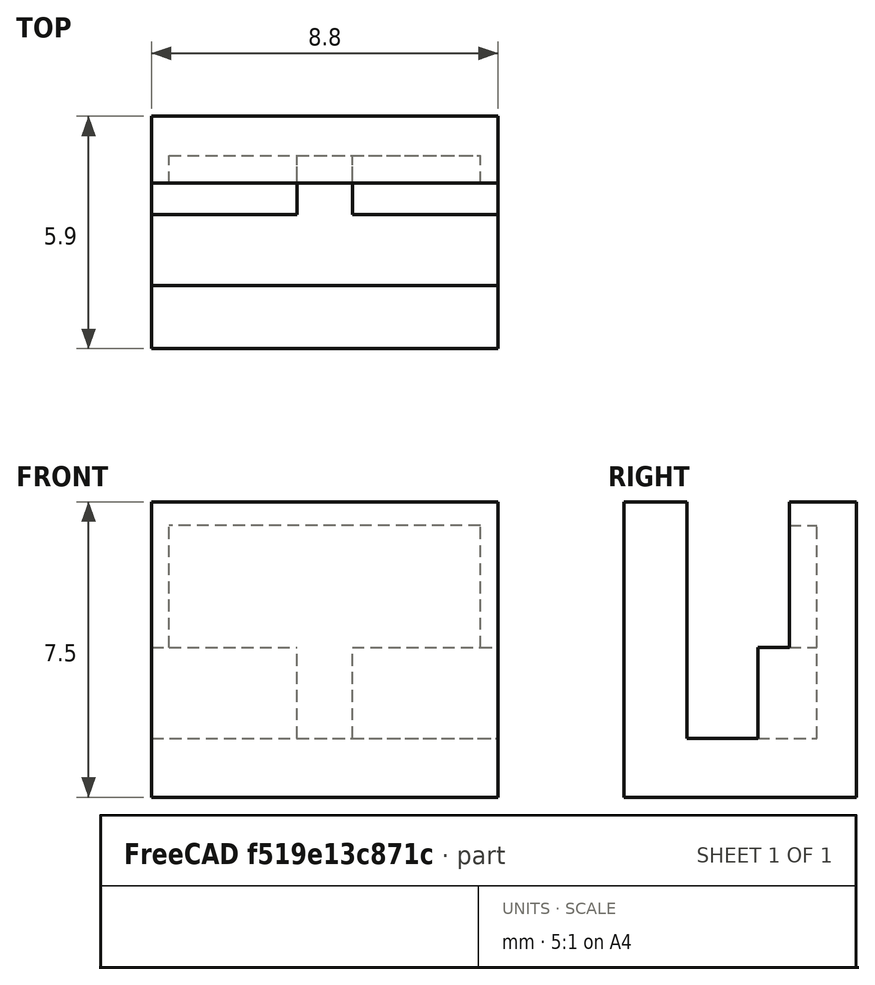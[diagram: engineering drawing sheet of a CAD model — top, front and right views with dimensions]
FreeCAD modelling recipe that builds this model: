
FCSTD DOCUMENT  (FreeCAD 0.19R)
Label: rad1o_switch
License: All rights reserved
LicenseURL: http://en.wikipedia.org/wiki/All_rights_reserved
objects: PartDesign::SubtractiveBox×4, PartDesign::AdditiveBox×1, PartDesign::Body×1
note: 11 computed .brp shape members not serialized (recipe doc carries the construction recipe); baked Part::Feature solids carry a one-line shape summary decoded from their .brp

FEATURE [PartDesign::AdditiveBox] Box
  AttacherType = Attacher::AttachEngine3D
  AttachmentOffset = pos=(0,0,-0.6) rot=(0,0,1;0rad)
  Height = 5.9
  Length = 7.5
  MapMode = 5
  Placement = pos=(0,0,-0.6) rot=(0,0,1;0rad)
  Support = -> [XY_Plane]
  Width = 8.8
  expr: Width = 6.5 + 1.5 + 0.80000000000000004
  expr: Length = 4.5 + 1.5 + 0.69999999999999996 + 0.80000000000000004
  expr: Height = 1 + 3.8999999999999999 + 1
FEATURE [PartDesign::SubtractiveBox] Box001
  AttacherType = Attacher::AttachEngine3D
  AttachmentOffset = pos=(1.5,0,1) rot=(0,0,1;0rad)
  BaseFeature = -> Box
  Height = 1.8
  Length = 10
  MapMode = 5
  Placement = pos=(1.5,0,1) rot=(0,0,1;0rad)
  Support = -> [XY_Plane]
  Width = 10
FEATURE [PartDesign::SubtractiveBox] Box002
  AttacherType = Attacher::AttachEngine3D
  AttachmentOffset = pos=(3.8,0.45,1) rot=(0,0,1;0rad)
  BaseFeature = -> Box001
  Height = 3.3
  Length = 3.1
  MapMode = 5
  Placement = pos=(3.8,0.45,1) rot=(0,0,1;0rad)
  Support = -> [XY_Plane]
  Width = 7.9
  expr: .AttachmentOffset.Base.x = 1.5 + 2.2999999999999998
FEATURE [PartDesign::SubtractiveBox] Box003
  AttacherType = Attacher::AttachEngine3D
  AttachmentOffset = pos=(1.5,3.7,2.8) rot=(0,0,1;0rad)
  BaseFeature = -> Box002
  Height = 1.5
  Length = 2.3
  MapMode = 5
  Placement = pos=(1.5,3.7,2.8) rot=(0,0,1;0rad)
  Support = -> [XY_Plane]
  Width = 1.4
FEATURE [PartDesign::SubtractiveBox] Box004
  AttacherType = Attacher::AttachEngine3D
  AttachmentOffset = pos=(3.8,0,1) rot=(0,0,1;0rad)
  BaseFeature = -> Box003
  Height = 2.6
  Length = 10
  MapMode = 2
  Placement = pos=(3.8,0,1) rot=(0,0,1;0rad)
  Support = -> [XY_Plane]
  Width = 10
FEATURE [PartDesign::Body] Body
  Group = -> [Box,Box001,Box002,Box003,Box004]
  Origin = -> Origin
  Placement = pos=(0,0,0) rot=(0.57735,0.57735,0.57735;4.18879rad)
  Tip = -> Box004
